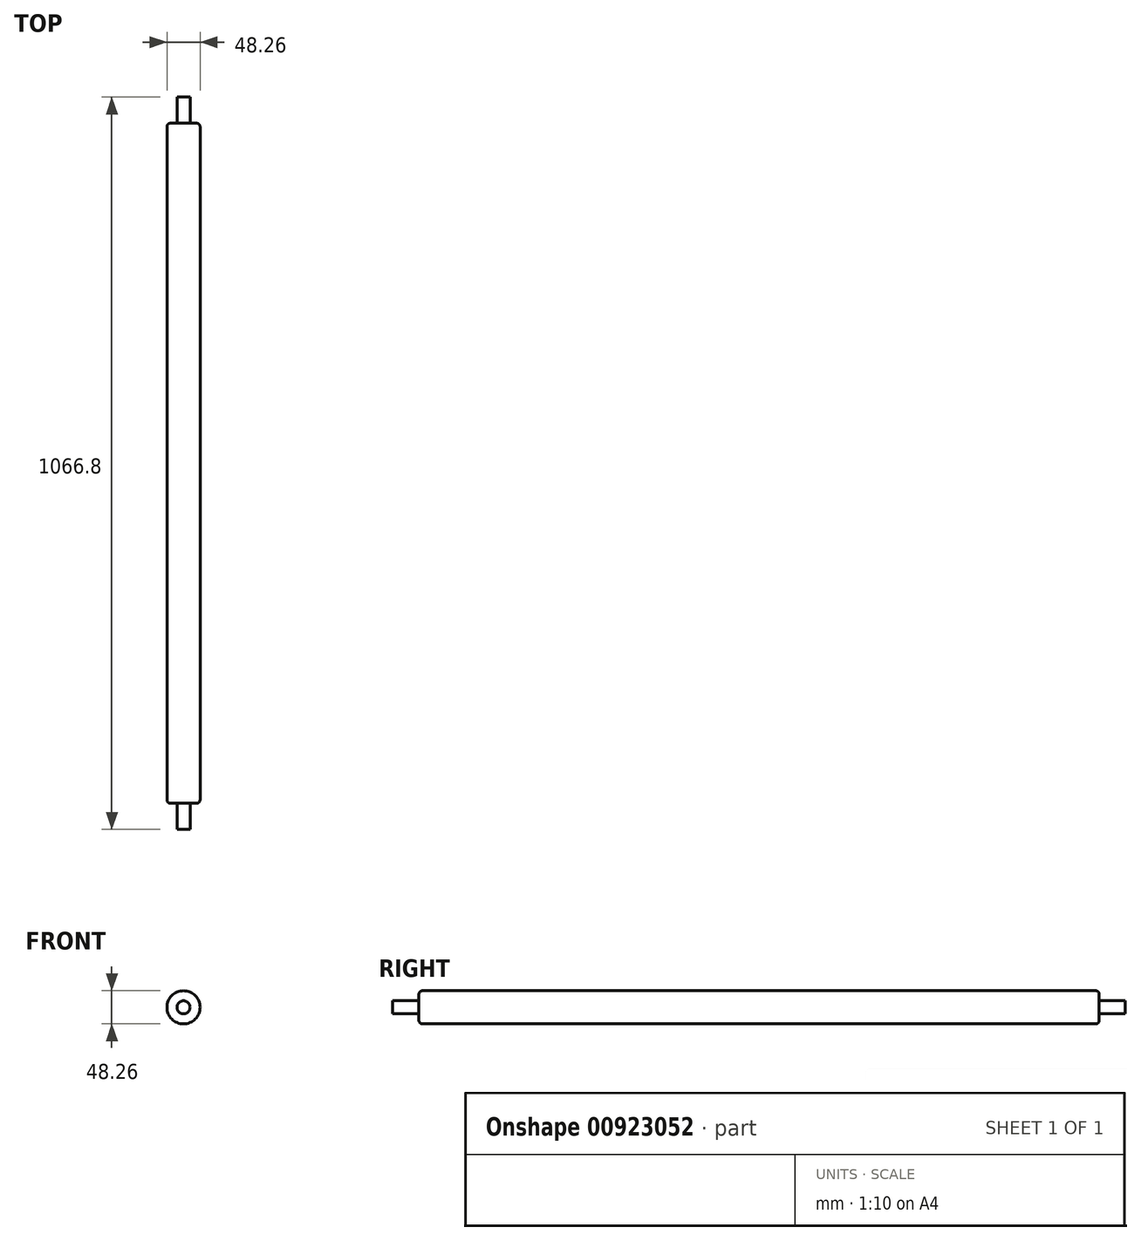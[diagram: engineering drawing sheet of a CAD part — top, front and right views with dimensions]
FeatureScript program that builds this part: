
annotation { "Feature Type Name" : "Feature", "Feature Type Description" : "" }
export const myFeature = defineFeature(function(context is Context, id is Id, definition is map)
    precondition{}
    {
        {
            var Q0;
            Q0=qCreatedBy(makeId("Front.planeOp"),FACE);
            var sketch = newSketch(context, id + "F0", { "sketchPlane" : qUnion([Q0])});
            skCircle(sketch, "E0", {"center": v(0, 0) * mm, "radius": 24.13 * mm});
            skSolve(sketch);
        }
        {
            var Q0;
            Q0=makeQuery(id+"F0.imprint","IMPRINT",FACE,{"disambiguationData":[TD([[makeQuery(id+"F0.imprint","IMPRINT",EDGE,{"derivedFrom":sQuery(id+"F0.wireOp",EDGE,"E0")}),1.0]])]});
            extrude(context, id + "F1", {"entities" : qUnion([Q0]), "oppositeDirection" : true, "depth" : 990.6 * mm, "offsetDistance" : 25 * mm});
        }
        {
            var Q0;
            Q0=makeQuery(id+"F1.opExtrude","CAP_FACE",FACE,{"disambiguationData":[OSD([sQuery(id+"F0.wireOp",EDGE,"E0")])],"isStart":true});
            var sketch = newSketch(context, id + "F2", { "sketchPlane" : qUnion([Q0])});
            skCircle(sketch, "E1", {"center": v(0, 0) * mm, "radius": 9.53 * mm});
            skSolve(sketch);
        }
        {
            var Q0;
            Q0=makeQuery(id+"F2.imprint","IMPRINT",FACE,{"disambiguationData":[TD([[makeQuery(id+"F2.imprint","IMPRINT",EDGE,{"derivedFrom":sQuery(id+"F2.wireOp",EDGE,"E1")}),1.0]])]});
            extrude(context, id + "F3", {"entities" : qUnion([Q0]), "operationType" : NewBodyOperationType.ADD, "depth" : 38.1 * mm, "offsetDistance" : 25 * mm});
        }
        {
            var Q0;
            Q0=makeQuery(id+"F1.opExtrude","CAP_FACE",FACE,{"disambiguationData":[OSD([sQuery(id+"F0.wireOp",EDGE,"E0")])],"isStart":false});
            var sketch = newSketch(context, id + "F4", { "sketchPlane" : qUnion([Q0])});
            skCircle(sketch, "E2", {"center": v(0, 0) * mm, "radius": 9.53 * mm});
            skSolve(sketch);
        }
        {
            var Q0;
            Q0=makeQuery(id+"F4.imprint","IMPRINT",FACE,{"disambiguationData":[TD([[makeQuery(id+"F4.imprint","IMPRINT",EDGE,{"derivedFrom":sQuery(id+"F4.wireOp",EDGE,"E2")}),1.0]])]});
            var Q1;
            Q1=sQuery(id+"F4.wireOp",EDGE,"E2");
            extrude(context, id + "F5", {"entities" : qUnion([Q0]), "surfaceEntities" : qUnion([Q1]), "depth" : 38.1 * mm, "offsetDistance" : 25 * mm});
        }
        {
            var Q0;
            Q0=makeQuery(id+"F1.opExtrude","CAP_EDGE",EDGE,{"disambiguationData":[OSD([sQuery(id+"F0.wireOp",EDGE,"E0")])],"isStart":true});
            var Q1;
            Q1=makeQuery(id+"F1.opExtrude","CAP_EDGE",EDGE,{"disambiguationData":[OSD([sQuery(id+"F0.wireOp",EDGE,"E0")])],"isStart":false});
            fillet(context, id + "F6", {"entities" : qUnion([Q0, Q1]), "radius" : 5 * mm, "tangentPropagation" : true, "allowEdgeOverflow" : false});
        }
    });
